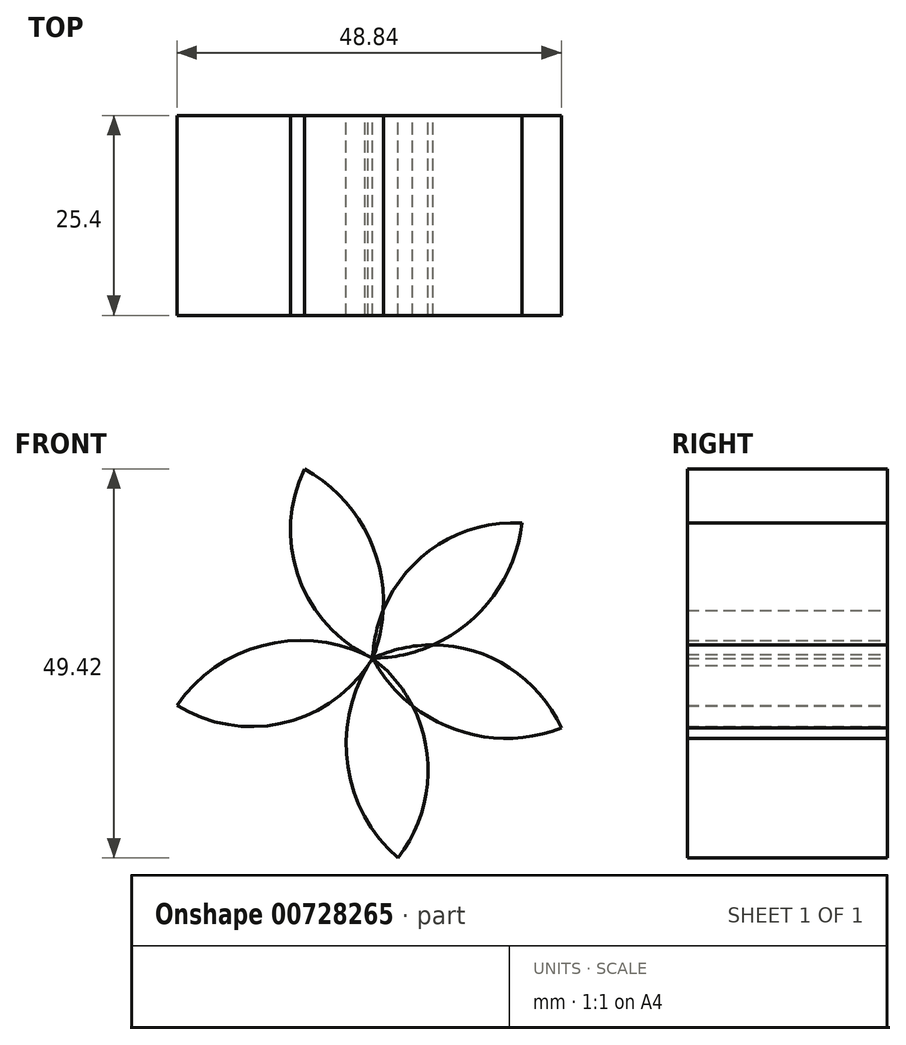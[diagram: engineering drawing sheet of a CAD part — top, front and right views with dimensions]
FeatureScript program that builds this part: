
annotation { "Feature Type Name" : "Feature", "Feature Type Description" : "" }
export const myFeature = defineFeature(function(context is Context, id is Id, definition is map)
    precondition{}
    {
        {
            var Q0;
            Q0=qCreatedBy(makeId("Front.planeOp"),FACE);
            var sketch = newSketch(context, id + "F0", { "sketchPlane" : qUnion([Q0])});
            skArc(sketch, "E0", {"start": v(18.94, 17.17) * mm, "mid": v(5.88, 12.55) * mm, "end": v(0, 0) * mm});
            skArc(sketch, "E1", {"start": v(0, 0) * mm, "mid": v(12.73, 5) * mm, "end": v(18.94, 17.17) * mm});
            skArc(sketch, "E2.1.0", {"start": v(23.98, -8.88) * mm, "mid": v(13.85, 0.58) * mm, "end": v(0, 0) * mm});
            skArc(sketch, "E2.1.1", {"start": v(0, 0) * mm, "mid": v(10.3, -8.98) * mm, "end": v(23.98, -8.88) * mm});
            skArc(sketch, "E2.2.0", {"start": v(3.2, -25.37) * mm, "mid": v(6.9, -12.01) * mm, "end": v(0, 0) * mm});
            skArc(sketch, "E2.2.1", {"start": v(0, 0) * mm, "mid": v(-3.21, -13.3) * mm, "end": v(3.2, -25.37) * mm});
            skPoint(sketch, "E2.center", {"position": v(0, 0) * mm});
            skLineSegment(sketch, "E2.anchor1", {"start": v(0, 0) * mm, "end": v(17.93, -0.75) * mm, "construction": true});
            skLineSegment(sketch, "E2.anchor2", {"start": v(0, 0) * mm, "end": v(-10.9, -14.26) * mm, "construction": true});
            skArc(sketch, "E3.1.0", {"start": v(-24.86, -5.97) * mm, "mid": v(-11.18, -8.19) * mm, "end": v(0, 0) * mm});
            skArc(sketch, "E3.1.1", {"start": v(0, 0) * mm, "mid": v(-13.56, 1.73) * mm, "end": v(-24.86, -5.97) * mm});
            skArc(sketch, "E3.2.0", {"start": v(-8.67, 24.05) * mm, "mid": v(-9.37, 10.21) * mm, "end": v(0, 0) * mm});
            skArc(sketch, "E3.2.1", {"start": v(0, 0) * mm, "mid": v(0.23, 13.67) * mm, "end": v(-8.67, 24.05) * mm});
            skLineSegment(sketch, "E3.anchor2", {"start": v(0, 0) * mm, "end": v(7.51, 16.3) * mm, "construction": true});
            skSolve(sketch);
        }
        {
            var Q0;
            {var subQ0=sQuery(id+"F0.wireOp",EDGE,"E1");var subQ1=sQuery(id+"F0.wireOp",EDGE,"E0");var subQ2=makeQuery(id+"F0.imprint","INTERSECT",VERTEX,{"derivedFrom":[subQ1,subQ0]});Q0=makeQuery(id+"F0.imprint","IMPRINT",FACE,{"disambiguationData":[TD([[makeQuery(id+"F0.imprint","IMPRINT",EDGE,{"disambiguationData":[TD([[subQ2,-1.0]])],"derivedFrom":subQ1}),1.0]])]});}
            var Q1;
            {var subQ1=sQuery(id+"F0.wireOp",EDGE,"E2.1.1");var subQ2=sQuery(id+"F0.wireOp",EDGE,"E2.1.0");var subQ6=makeQuery(id+"F0.imprint","INTERSECT",VERTEX,{"derivedFrom":[subQ2,subQ1]});Q1=makeQuery(id+"F0.imprint","IMPRINT",FACE,{"disambiguationData":[TD([[makeQuery(id+"F0.imprint","IMPRINT",EDGE,{"disambiguationData":[TD([[subQ6,-1.0]])],"derivedFrom":subQ2}),1.0]])]});}
            var Q2;
            {var subQ1=sQuery(id+"F0.wireOp",EDGE,"E2.2.1");var subQ2=sQuery(id+"F0.wireOp",EDGE,"E2.2.0");var subQ6=makeQuery(id+"F0.imprint","INTERSECT",VERTEX,{"derivedFrom":[subQ2,subQ1]});Q2=makeQuery(id+"F0.imprint","IMPRINT",FACE,{"disambiguationData":[TD([[makeQuery(id+"F0.imprint","IMPRINT",EDGE,{"disambiguationData":[TD([[subQ6,-1.0]])],"derivedFrom":subQ2}),1.0]])]});}
            var Q3;
            {var subQ1=sQuery(id+"F0.wireOp",EDGE,"E3.1.1");var subQ2=sQuery(id+"F0.wireOp",EDGE,"E3.1.0");var subQ6=makeQuery(id+"F0.imprint","INTERSECT",VERTEX,{"derivedFrom":[subQ2,subQ1]});Q3=makeQuery(id+"F0.imprint","IMPRINT",FACE,{"disambiguationData":[TD([[makeQuery(id+"F0.imprint","IMPRINT",EDGE,{"disambiguationData":[TD([[subQ6,-1.0]])],"derivedFrom":subQ2}),1.0]])]});}
            var Q4;
            {var subQ0=sQuery(id+"F0.wireOp",EDGE,"E3.2.1");var subQ1=sQuery(id+"F0.wireOp",EDGE,"E3.2.0");var subQ6=makeQuery(id+"F0.imprint","INTERSECT",VERTEX,{"derivedFrom":[subQ1,subQ0]});Q4=makeQuery(id+"F0.imprint","IMPRINT",FACE,{"disambiguationData":[TD([[makeQuery(id+"F0.imprint","IMPRINT",EDGE,{"disambiguationData":[TD([[subQ6,-1.0]])],"derivedFrom":subQ1}),1.0]])]});}
            extrude(context, id + "F1", {"entities" : qUnion([Q0, Q1, Q2, Q3, Q4]), "depth" : 25.4 * mm, "offsetDistance" : 25.4 * mm});
        }
    });
